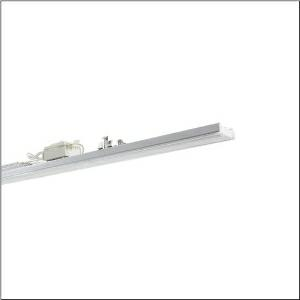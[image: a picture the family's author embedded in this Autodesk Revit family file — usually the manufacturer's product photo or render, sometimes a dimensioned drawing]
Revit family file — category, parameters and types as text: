
# Revit family: licross_r__21_recessed_ho_52tl12de475m_fe62
name_source: partatom
category: Lighting Fixtures
units: mm (PartAtom-declared; Revit-internal decimal feet)

## family parameters
Cut with Voids When Loaded = No
Host = Face
Light Source = No
Part Type = Normal
Room Calculation Point = No
Round Connector Dimension = Use Diameter
Shared = No

## types (1)
- --- (1 x LED, 7500 lm, 44.1 W, 4000K)
    Apparent Load = 44 VA
    CIE Flux Codes = 69 91 98 100 100
    Color Rendering = 80
    Color Temperature = 4000K
    Default Elevation = 1800 mm
    Description = Licross® 21 Recessed HO, luminaire insert, of sheet steel, galvanised, coil coated, white, length: 750mm, width: 66mm, height: 67mm, LED rated luminous flux: 7.500lm, light colour: 840, control gear: DALI 2, with plug, 5-pole, with phase selection, mains connection: 220..240V, AC, 50/60Hz, rated input power: 44W, internal wiring halogen-free, primary light control with lens, of plastic, primary optical cover: cover, of PMMA, light emission: direct distribution, primary light characteristic: symmetric, protection rating (complete): IP40, insulation class (complete): insulation class I (protective earthing), certification: CE, ENEC, VDE, UKCA, protection symbol: D if used in an environment without relevant dust loads with corresponding accessories, impact resistance: IK06, permissible ambient temperature for indoor applications: -25..+30°C, corresponds to IFS (International Featured Standards) requirements for safety and quality in the food industry, reducing of maximum allowable ambient temperature of 5°C with ceiling mounting, LABS conformity tested according to VDMA 24364:2018-05, packaging unit: 1 piece
    Height = 58 mm
    Lamp = 1 x LED
    Lamp Light Flux = 7500 lm
    Lamp Power = 44.1 W
    Lamp count = 1
    Length = 750 mm
    Luminous efficacy = 170 lm/W
    Manufacturer = Siteco
    ModVariant = No
    Model = 52TL12DE475M
    Mounting Place = Ceiling
    Mounting Type = Pendant
    Number of Poles = 1
    OnlyDefault = Yes
    Power Factor = 1
    Product Name = Licross® 21 Recessed HO
    Product group = luminaire insert | ceiling pendant
    ProductGroupID = 902
    Protection Class = Protection class I
    Protection Degree = IP 40
    RLX_Detail_Level = 1
    RLX_Emergency_Light_Flux = 0 lm
    RLX_Emergency_Type = 0
    RLX_Emergency_Type_DB = No
    RlxData = <blob elided: 29677 chars, md5=62b12913>
    Socket = socket
    Standby Power = 0 W
    System Light Flux = 7500 lm
    System Power = 44 W
    Type Comments = factory setting: luminous flux: 100 % | dim-lin: 254 | 484 mA
    Type Image = l_1296930.jpg
    URL = http://relux.com
    VarID = @adj_138289
    Voltage = 0 V
    Weight = 0.00 kg
    Width = 66 mm

## geometry (parser evidence)
native form markers: Blend x4, Sweep x10
no freeform markers — native parametric forms only
